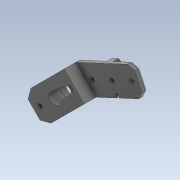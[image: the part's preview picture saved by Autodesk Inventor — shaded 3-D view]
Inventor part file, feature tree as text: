
AUTODESK INVENTOR PART (.ipt)
format: ipt  version: 2020 (Build 240168000, 168)  size: 394,752 bytes
history: native  units: in
note: dims shown in document units (in); Inventor stores cm internally (conversion verified against a paired STEP export)
features: sketch x12, other x6, extrude x6, projected_geometry x4, reference x1
ambient origin geometry x8: Origin, YZ Plane, XZ Plane, XY Plane, X Axis, Y Axis, Z Axis, Center Point
bodies: Solid1 (feature_tree)
feature tree (29):
  other  "TibiaTop.ipt"
  extrude  "Extrusion1"  Depth=0.3937in TaperAngle=0.0deg
  extrude  "Extrusion2"  Depth=0.1969in
  extrude  "Extrusion3"  Depth=0.0398in
  extrude  "Extrusion8"  Depth=0.1575in
  extrude  "Extrusion9"  Depth=0.4761in
  extrude  "Extrusion10"  Depth=0.0059in
  other  "Solid2::TibiaTop.ipt"
  other  "TaggingFeature1"
  sketch  "Sketch1"  dims[d0=0.3937in d1=0.3937in d2=0.0in]
  sketch  "Sketch9"  dims[d5=0.0398in d6=0.0398in]
  sketch  "Sketch10"  dims[d8=0.6142in d9=0.1575in]
  sketch  "Sketch11"  dims[d10=0.4761in d11=0.4761in]
  sketch  "Sketch15"  dims[d15=0.3307in d16=0.0in]
  sketch  "Sketch25"  dims[d34=0.0787in d35=0.0in]
  sketch  "Sketch26"  dims[d36=0.2756in d37=0.0787in d38=0.0in d39=0.0039in d40=0.3937in d41=0.0in d24=0.0197in d25=0.0344in d26=0.0197in d27=0.0344in d42=0.0197in d43=0.0344in]
  sketch  "Sketch8"  dims[d3=0.2835in d4=0.1969in]
  sketch  "Sketch12"  dims[d12=0.0059in d13=0.0059in]
  reference  "Reference1"
  sketch  "Sketch13"  dims[d14=0.0059in]
  projected_geometry  "Projected Loop1"
  projected_geometry  "Projected Loop6"
  sketch  "Sketch20"  dims[d17=0.3307in d18=0.0in]
  projected_geometry  "Projected Loop7"
  sketch  "Sketch21"  dims[d33=0.2756in]
  projected_geometry  "Projected Loop8"
  parser-record x1  (decoder bookkeeping rows leaked as tree rows — omitted from the tree; the rows remain in map.json)
  other  "LegDemoRight.iam"
  other  "TibiaTop:1"
note: 1 file-system path scrubbed to <path> (originals preserved in map.json)
